# Revit family: Sanitary_Shower-screens_Duscholux_D5Custom20_Slider-twin-door-bath
name_source: partatom
category: Aparatos sanitarios
units: mm (PartAtom-declared; Revit-internal decimal feet)

## family parameters
Compartido = No
Corte con vacíos al cargar = No
Cota de conector redondo = Diámetro de uso
Número OmniClass = 23.45.00.00
Punto de cálculo de habitación = No
Se basa en plano de trabajo = No
Siempre vertical = Sí
Tipo de pieza = Normal
Título OmniClass = Sanitary, Laundry, and Cleaning Equipment

## types (3) — shared parameters
Bath Heigth = 400 mm  [stored 1.31234 ft]
Certified Quality UNE EN 14428 = http://www.duscholux.es
Combinations = Lateral 90°
Components = Eropean components
Configuration enclosure = http://configuratumampara.duscholux.es
Código de montaje = C1030200
Descripción = 2 fixed segments + slider twin doors
Environmental Management ISO 14001 = ECOEMBES Certificate
Fabricante = Duscholux Ibérica, S.A.
Fact Sheet = https://duscholux.blob.core.windows.net
Glass Material = Glass_Material-Duscholux
Glass in Building UNE EN 12150 = CE Conformity marking
Handle Height = 1200 mm
Height = 1600 mm  [stored 5.24934 ft]
Image = https://duscholux.es
Maintenance and Cleaning = http://www.duscholux.es
Max Height = 1600 mm  [stored 5.24934 ft]
Min Max Width = 1800 mm  [stored 5.90551 ft]
Modelo = D5 Custom20
Opening Door = 5 mm  [stored 0.0164042 ft]
Opening System = Sliding
Opening System Image = https://duscholux.es
Optional = Towel rail / Shelf / Customizable Uper profile guide
Products = http://www.duscholux.es
Ref. = UAW
Series = D5
Sliding Door Width = 459 mm  [stored 1.50591 ft]
Technical Inspection Certificate (Applus) = http://www.duscholux.es
Thickness Safety Glass Fixed Panel = 8 mm  [stored 0.0262467 ft]
Thickness Safety Glass Sliding = 8 mm  [stored 0.0262467 ft]
URL = http://www.duscholux.es
Width = 1800 mm  [stored 5.90551 ft]
zero-valued in all types: Opening Percentage

## per-type parameters (varying)
| type | Accesories Material | Frame Material | Handle Material | Uper profile guide |
| Matte Silver Aluminium Finish | Anodized Aluminium_Duscholux Material-Platinum Finish | Anodized Aluminium_Duscholux Material-Matte Silver Finish | Zamac_Duscholux Material-Chrome Finish | Anodized Aluminium_Duscholux Material-Matte Silver Finish |
| Platinum Aluminium Finish | Anodized Aluminium_Duscholux Material-Platinum Finish | Anodized Aluminium_Duscholux Material-Platinum Finish | Zamac_Duscholux Material-Chrome Finish | Anodized Aluminium_Duscholux Material-Platinum Finish |
| Black Aluminium Finish | Anodized Aluminium_Duscholux Material-Black Finish | Anodized Aluminium_Duscholux Material-Black Finish | Anodized Aluminium_Duscholux Material-Black Finish | Anodized Aluminium_Duscholux Material-Black Finish |

note: [stored X ft] marks values corroborated as IEEE doubles in the binary element streams (Revit-internal decimal feet)
